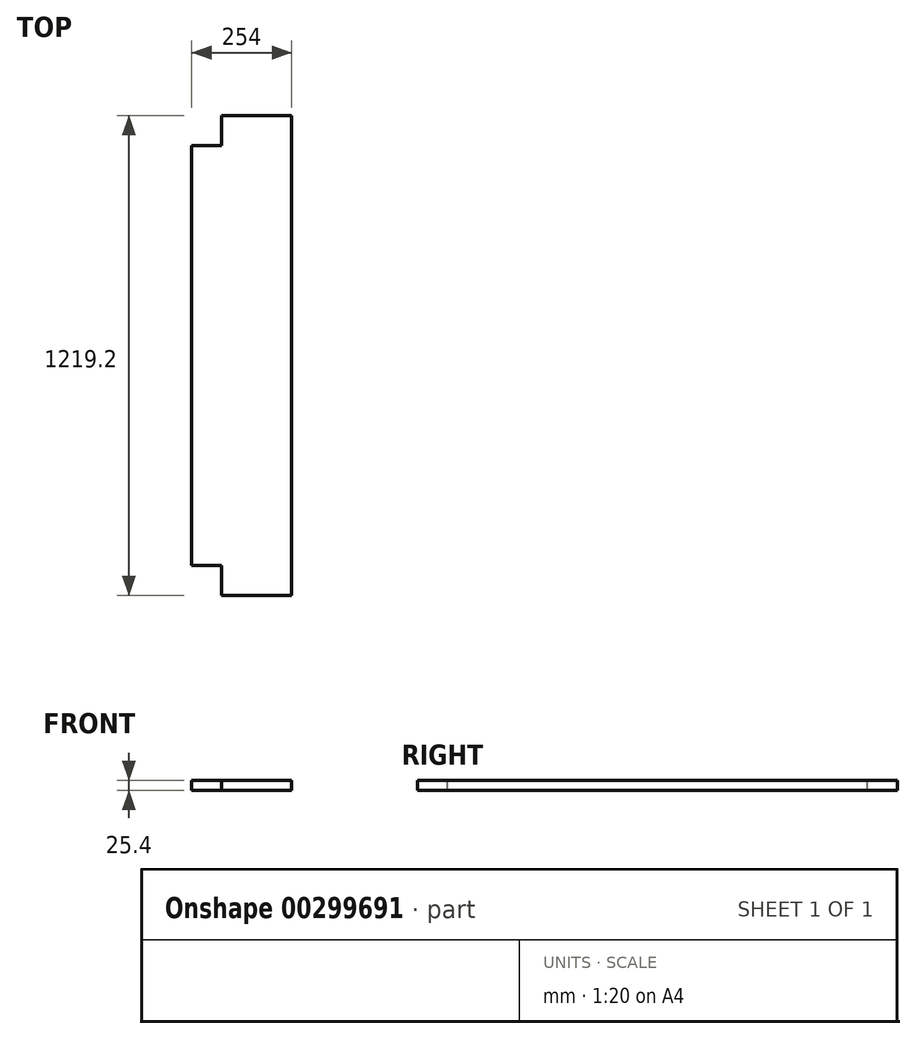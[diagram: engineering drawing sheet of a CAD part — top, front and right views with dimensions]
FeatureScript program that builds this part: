
annotation { "Feature Type Name" : "Feature", "Feature Type Description" : "" }
export const myFeature = defineFeature(function(context is Context, id is Id, definition is map)
    precondition{}
    {
        {
            var Q0;
            Q0=qCreatedBy(makeId("Top.planeOp"),FACE);
            var sketch = newSketch(context, id + "F0", { "sketchPlane" : qUnion([Q0])});
            skLineSegment(sketch, "E0.bottom", {"start": v(-128.89, 936.06) * mm, "end": v(125.11, 936.06) * mm});
            skLineSegment(sketch, "E0.top", {"start": v(-128.89, -283.14) * mm, "end": v(125.11, -283.14) * mm});
            skLineSegment(sketch, "E0.left", {"start": v(-128.89, 936.06) * mm, "end": v(-128.89, -283.14) * mm});
            skLineSegment(sketch, "E0.right", {"start": v(125.11, 936.06) * mm, "end": v(125.11, -283.14) * mm});
            skSolve(sketch);
        }
        {
            var Q0;
            Q0=qSketchRegion(id+"F0",true);
            extrude(context, id + "F1", {"entities" : qUnion([Q0]), "depth" : 25.4 * mm});
        }
        {
            var Q0;
            Q0=makeQuery(id+"F1.opExtrude","CAP_FACE",FACE,{"disambiguationData":[OSD([sQuery(id+"F0.wireOp",EDGE,"E0.bottom"),sQuery(id+"F0.wireOp",EDGE,"E0.top"),sQuery(id+"F0.wireOp",EDGE,"E0.left"),sQuery(id+"F0.wireOp",EDGE,"E0.right")])],"isStart":false});
            var sketch = newSketch(context, id + "F2", { "sketchPlane" : qUnion([Q0])});
            skLineSegment(sketch, "E1.bottom", {"start": v(-128.89, 936.06) * mm, "end": v(-52.69, 936.06) * mm});
            skLineSegment(sketch, "E1.top", {"start": v(-128.89, 859.86) * mm, "end": v(-52.69, 859.86) * mm});
            skLineSegment(sketch, "E1.left", {"start": v(-128.89, 936.06) * mm, "end": v(-128.89, 859.86) * mm});
            skLineSegment(sketch, "E1.right", {"start": v(-52.69, 936.06) * mm, "end": v(-52.69, 859.86) * mm});
            skLineSegment(sketch, "E2.bottom", {"start": v(-128.89, -283.14) * mm, "end": v(-52.69, -283.14) * mm});
            skLineSegment(sketch, "E2.top", {"start": v(-128.89, -206.94) * mm, "end": v(-52.69, -206.94) * mm});
            skLineSegment(sketch, "E2.left", {"start": v(-128.89, -283.14) * mm, "end": v(-128.89, -206.94) * mm});
            skLineSegment(sketch, "E2.right", {"start": v(-52.69, -283.14) * mm, "end": v(-52.69, -206.94) * mm});
            skSolve(sketch);
        }
        {
            var Q0;
            Q0 = qSketchRegion(id + "F2", true);
            extrude(context, id + "F3", {"entities" : qUnion([Q0]), "operationType" : NewBodyOperationType.REMOVE, "oppositeDirection" : true, "depth" : 25.4 * mm});
        }
    });
